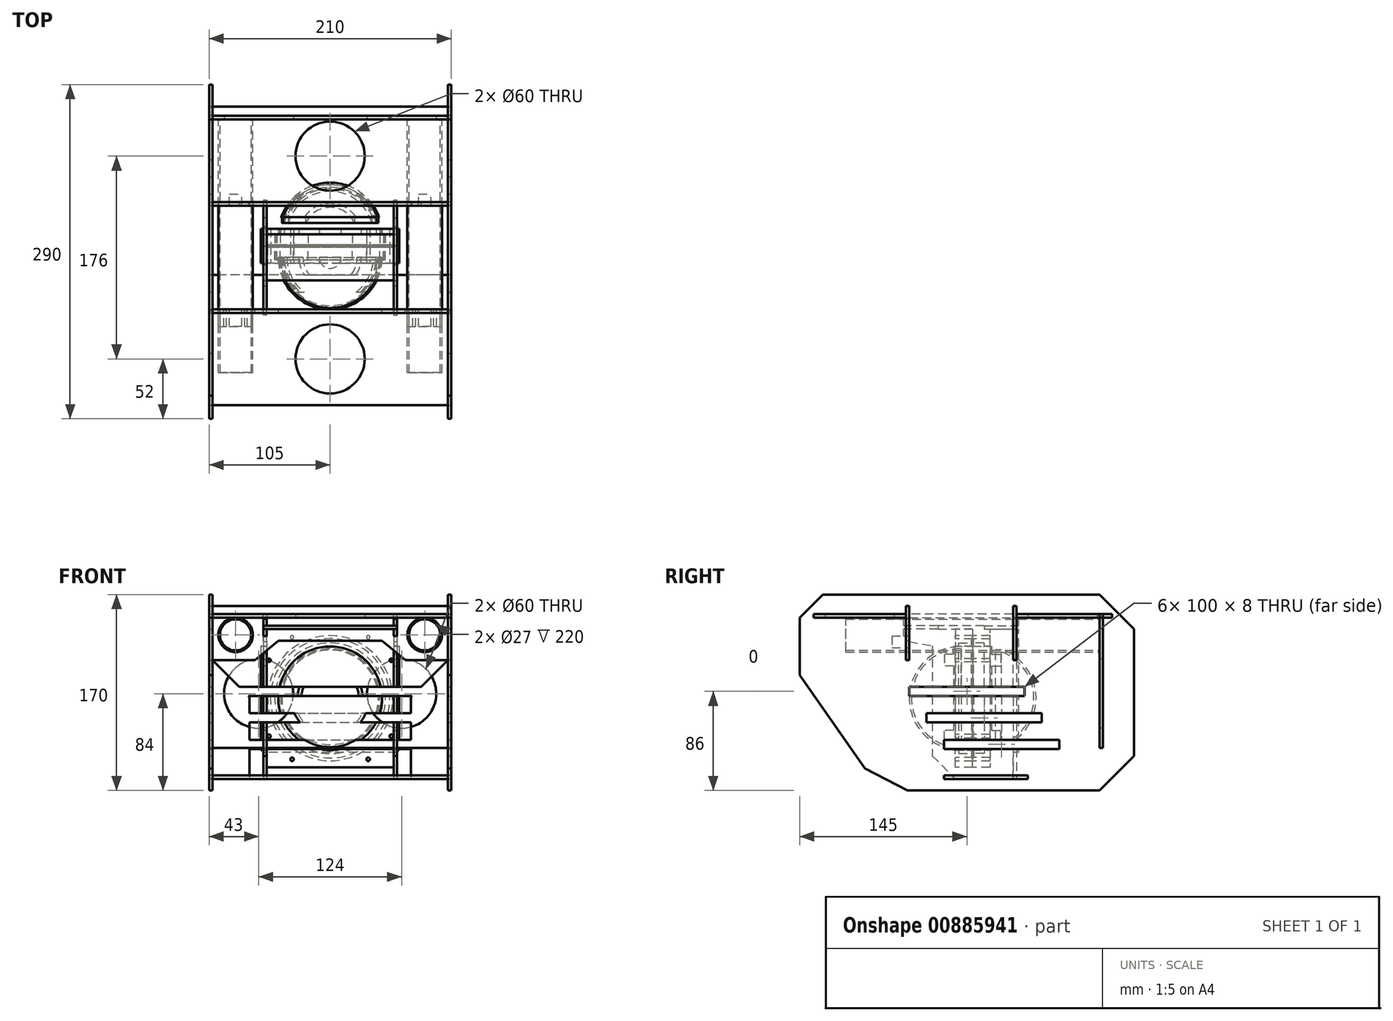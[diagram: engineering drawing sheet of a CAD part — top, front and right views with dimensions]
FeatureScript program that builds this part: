
annotation { "Feature Type Name" : "Feature", "Feature Type Description" : "" }
export const myFeature = defineFeature(function(context is Context, id is Id, definition is map)
    precondition{}
    {
        {
            var Q0;
            Q0=qCreatedBy(makeId("Front.planeOp"),FACE);
            var sketch = newSketch(context, id + "F0", { "sketchPlane" : qUnion([Q0])});
            skArc(sketch, "E0", {"start": v(0, 45) * mm, "mid": v(-45, 0) * mm, "end": v(0, -45) * mm});
            skLineSegment(sketch, "E1", {"start": v(0, 45) * mm, "end": v(0, -45) * mm});
            skSolve(sketch);
        }
        {
            var Q0;
            Q0=makeQuery(id+"F0.imprint","IMPRINT",FACE,{"disambiguationData":[TD([[makeQuery(id+"F0.imprint","IMPRINT",EDGE,{"derivedFrom":sQuery(id+"F0.wireOp",EDGE,"E0")}),1.0]])]});
            var Q1;
            Q1=sQuery(id+"F0.wireOp",EDGE,"E1");
            revolve(context, id + "F1", {"surfaceOperationType" : NewSurfaceOperationType.NEW, "entities" : qUnion([Q0]), "axis" : qUnion([Q1]), "revolveType" : RevolveType.ONE_DIRECTION, "oppositeDirection" : true, "angle" : 180 * degree});
        }
        {
            var Q0;
            Q0=qCreatedBy(makeId("Front.planeOp"),FACE);
            var sketch = newSketch(context, id + "F2", { "sketchPlane" : qUnion([Q0])});
            skArc(sketch, "E2", {"start": v(0, 43) * mm, "mid": v(-43, 0) * mm, "end": v(0, -43) * mm});
            skLineSegment(sketch, "E3", {"start": v(0, 43) * mm, "end": v(0, -43) * mm});
            skSolve(sketch);
        }
        {
            var Q0;
            Q0=makeQuery(id+"F2.imprint","IMPRINT",FACE,{"disambiguationData":[TD([[makeQuery(id+"F2.imprint","IMPRINT",EDGE,{"derivedFrom":sQuery(id+"F2.wireOp",EDGE,"E2")}),1.0]])]});
            var Q1;
            Q1=sQuery(id+"F2.wireOp",EDGE,"E3");
            revolve(context, id + "F3", {"operationType" : NewBodyOperationType.REMOVE, "surfaceOperationType" : NewSurfaceOperationType.NEW, "entities" : qUnion([Q0]), "axis" : qUnion([Q1]), "revolveType" : RevolveType.FULL, "oppositeDirection" : true});
        }
        {
            var Q0;
            Q0=qCreatedBy(makeId("Front.planeOp"),FACE);
            var sketch = newSketch(context, id + "F4", { "sketchPlane" : qUnion([Q0])});
            skCircle(sketch, "E4", {"center": v(0, 0) * mm, "radius": 43 * mm});
            skCircle(sketch, "E5", {"center": v(0, 0) * mm, "radius": 48 * mm});
            skSolve(sketch);
        }
        {
            var Q0;
            Q0 = qSketchRegion(id + "F4", true);
            extrude(context, id + "F5", {"entities" : qUnion([Q0]), "operationType" : NewBodyOperationType.ADD, "depth" : 2 * mm, "offsetDistance" : 25 * mm});
        }
        {
            var Q0;
            Q0=qCreatedBy(makeId("Front.planeOp"),FACE);
            var sketch = newSketch(context, id + "F6", { "sketchPlane" : qUnion([Q0])});
            skCircle(sketch, "E6", {"center": v(0, 0) * mm, "radius": 45 * mm});
            skLineSegment(sketch, "E7.bottom", {"start": v(60, 60) * mm, "end": v(-60, 60) * mm});
            skLineSegment(sketch, "E7.top", {"start": v(60, -60) * mm, "end": v(-60, -60) * mm});
            skLineSegment(sketch, "E7.left", {"start": v(60, 60) * mm, "end": v(60, -60) * mm});
            skLineSegment(sketch, "E7.right", {"start": v(-60, 60) * mm, "end": v(-60, -60) * mm});
            skSolve(sketch);
        }
        {
            var Q0;
            Q0 = qSketchRegion(id + "F6", true);
            extrude(context, id + "F7", {"entities" : qUnion([Q0]), "depth" : 5 * mm, "offsetDistance" : 25 * mm, "hasSecondDirection" : true, "secondDirectionOppositeDirection" : true, "secondDirectionDepth" : 10 * mm});
        }
        {
            var Q0;
            Q0=makeQuery(id+"F7.opExtrude","CAP_FACE",FACE,{"disambiguationData":[OSD([sQuery(id+"F6.wireOp",EDGE,"E6"),sQuery(id+"F6.wireOp",EDGE,"E7.bottom"),sQuery(id+"F6.wireOp",EDGE,"E7.top"),sQuery(id+"F6.wireOp",EDGE,"E7.left"),sQuery(id+"F6.wireOp",EDGE,"E7.right")])],"isStart":true});
            var sketch = newSketch(context, id + "F8", { "sketchPlane" : qUnion([Q0])});
            skCircle(sketch, "E8", {"center": v(0, 0) * mm, "radius": 45 * mm});
            skCircle(sketch, "E9", {"center": v(0, 0) * mm, "radius": 48 * mm});
            skSolve(sketch);
        }
        {
            var Q0;
            Q0 = qSketchRegion(id + "F8", true);
            extrude(context, id + "F9", {"entities" : qUnion([Q0]), "operationType" : NewBodyOperationType.REMOVE, "oppositeDirection" : true, "depth" : 12 * mm, "offsetDistance" : 25 * mm});
        }
        {
            var Q0;
            Q0=qCreatedBy(makeId("Front.planeOp"),FACE);
            var sketch = newSketch(context, id + "F10", { "sketchPlane" : qUnion([Q0])});
            skCircle(sketch, "E10", {"center": v(53, -33) * mm, "radius": 1.5 * mm});
            skCircle(sketch, "E11", {"center": v(33, -53) * mm, "radius": 1.5 * mm});
            skCircle(sketch, "E12.MirrorC", {"center": v(53, 33) * mm, "radius": 1.5 * mm});
            skCircle(sketch, "E13.MirrorC", {"center": v(33, 53) * mm, "radius": 1.5 * mm});
            skCircle(sketch, "E14.MirrorC", {"center": v(-33, -53) * mm, "radius": 1.5 * mm});
            skCircle(sketch, "E15.MirrorC", {"center": v(-53, -33) * mm, "radius": 1.5 * mm});
            skCircle(sketch, "E16.MirrorC", {"center": v(-53, 33) * mm, "radius": 1.5 * mm});
            skCircle(sketch, "E17.MirrorC", {"center": v(-33, 53) * mm, "radius": 1.5 * mm});
            skSolve(sketch);
        }
        {
            var Q0;
            Q0 = qSketchRegion(id + "F10", true);
            extrude(context, id + "F11", {"entities" : qUnion([Q0]), "operationType" : NewBodyOperationType.REMOVE, "endBound" : BoundingType.SYMMETRIC, "oppositeDirection" : true, "depth" : 50 * mm, "offsetDistance" : 25 * mm});
        }
        {
            var Q0;
            Q0=makeQuery(id+"F7.opExtrude","CAP_FACE",FACE,{"disambiguationData":[OSD([sQuery(id+"F6.wireOp",EDGE,"E6"),sQuery(id+"F6.wireOp",EDGE,"E7.bottom"),sQuery(id+"F6.wireOp",EDGE,"E7.top"),sQuery(id+"F6.wireOp",EDGE,"E7.left"),sQuery(id+"F6.wireOp",EDGE,"E7.right")])],"isStart":true});
            var sketch = newSketch(context, id + "F12", { "sketchPlane" : qUnion([Q0])});
            skCircle(sketch, "E18", {"center": v(0, 0) * mm, "radius": 69 * mm});
            skSolve(sketch);
        }
        {
            var Q0;
            Q0=qCreatedBy(makeId("Top.planeOp"),FACE);
            var sketch = newSketch(context, id + "F13", { "sketchPlane" : qUnion([Q0])});
            skCircle(sketch, "E19", {"center": v(53, 10) * mm, "radius": 1.25 * mm, "construction": true});
            skLineSegment(sketch, "E20.bottom", {"start": v(54.25, 9) * mm, "end": v(51.75, 9) * mm});
            skLineSegment(sketch, "E20.top", {"start": v(54.25, 11) * mm, "end": v(51.75, 11) * mm});
            skLineSegment(sketch, "E20.left", {"start": v(54.25, 9) * mm, "end": v(54.25, 11) * mm});
            skLineSegment(sketch, "E20.right", {"start": v(51.75, 9) * mm, "end": v(51.75, 11) * mm});
            skSolve(sketch);
        }
        {
            var Q0;
            Q0 = qSketchRegion(id + "F13", true);
            var Q1;
            Q1=sQuery(id+"F12.wireOp",EDGE,"E18");
            sweep(context, id + "F14", {"operationType" : NewBodyOperationType.REMOVE, "profiles" : qUnion([Q0]), "path" : qUnion([Q1])});
        }
        {
            var Q0;
            {var subQ0=sQuery(id+"F6.wireOp",EDGE,"E7.right");var subQ1=sQuery(id+"F6.wireOp",EDGE,"E7.left");var subQ2=sQuery(id+"F6.wireOp",EDGE,"E7.top");var subQ3=sQuery(id+"F6.wireOp",EDGE,"E7.bottom");Q0=makeQuery(id+"F14.boolean.opBoolean","SPLIT",FACE,{"disambiguationData":[TD([makeQuery(id+"F7.opExtrude","SWEPT_FACE",FACE,{"disambiguationData":[OSD([subQ3])]})])],"derivedFrom":makeQuery(id+"F7.opExtrude","CAP_FACE",FACE,{"disambiguationData":[OSD([sQuery(id+"F6.wireOp",EDGE,"E6"),subQ3,subQ2,subQ1,subQ0])],"isStart":true})});}
            var sketch = newSketch(context, id + "F15", { "sketchPlane" : qUnion([Q0])});
            skLineSegment(sketch, "E21.bottom", {"start": v(-60, -60) * mm, "end": v(60, -60) * mm});
            skLineSegment(sketch, "E21.top", {"start": v(-60, 60) * mm, "end": v(60, 60) * mm});
            skLineSegment(sketch, "E21.left", {"start": v(-60, -60) * mm, "end": v(-60, 60) * mm});
            skLineSegment(sketch, "E21.right", {"start": v(60, -60) * mm, "end": v(60, 60) * mm});
            skCircle(sketch, "E22", {"center": v(0, 0) * mm, "radius": 60 * mm});
            skSolve(sketch);
        }
        {
            var Q0;
            Q0 = qSketchRegion(id + "F15", true);
            extrude(context, id + "F16", {"entities" : qUnion([Q0]), "depth" : 15 * mm, "offsetDistance" : 25 * mm});
        }
        {
            var Q0;
            Q0=qCreatedBy(makeId("Front.planeOp"),FACE);
            cPlane(context, id + "F17", {"entities" : qUnion([Q0]), "cplaneType" : CPlaneType.OFFSET, "offset" : 20 * mm, "oppositeDirection" : true, "width" : 150 * mm, "height" : 150 * mm});
        }
        {
            var Q0;
            Q0 = qSketchRegion(id + "F8", true);
            extrude(context, id + "F18", {"entities" : qUnion([Q0]), "operationType" : NewBodyOperationType.REMOVE, "depth" : 12 * mm, "offsetDistance" : 25 * mm});
        }
        {
            var Q0;
            Q0=qCreatedBy(id+"F17.planeOp",FACE);
            var sketch = newSketch(context, id + "F19", { "sketchPlane" : qUnion([Q0])});
            skArc(sketch, "E23", {"start": v(-45, 0) * mm, "mid": v(0, -45) * mm, "end": v(45, 0) * mm});
            skLineSegment(sketch, "E24", {"start": v(-45, 0) * mm, "end": v(45, 0) * mm});
            skSolve(sketch);
        }
        {
            var Q0;
            Q0 = qSketchRegion(id + "F19", true);
            var Q1;
            Q1=sQuery(id+"F19.wireOp",EDGE,"E24");
            revolve(context, id + "F20", {"surfaceOperationType" : NewSurfaceOperationType.NEW, "entities" : qUnion([Q0]), "axis" : qUnion([Q1]), "revolveType" : RevolveType.ONE_DIRECTION, "angle" : 180 * degree});
        }
        {
            var Q0;
            Q0=makeQuery(id+"F20.opRevolve","CAP_FACE",FACE,{"disambiguationData":[OSD([sQuery(id+"F19.wireOp",EDGE,"E23"),sQuery(id+"F19.wireOp",EDGE,"E24")])],"isStart":true});
            var sketch = newSketch(context, id + "F21", { "sketchPlane" : qUnion([Q0])});
            skArc(sketch, "E25", {"start": v(-43, 0) * mm, "mid": v(0, -43) * mm, "end": v(43, 0) * mm});
            skLineSegment(sketch, "E26", {"start": v(-43, 0) * mm, "end": v(43, 0) * mm});
            skSolve(sketch);
        }
        {
            var Q0;
            Q0 = qSketchRegion(id + "F21", true);
            var Q1;
            Q1=sQuery(id+"F21.wireOp",EDGE,"E26");
            revolve(context, id + "F22", {"operationType" : NewBodyOperationType.REMOVE, "surfaceOperationType" : NewSurfaceOperationType.NEW, "entities" : qUnion([Q0]), "axis" : qUnion([Q1]), "revolveType" : RevolveType.FULL, "oppositeDirection" : true});
        }
        {
            var Q0;
            Q0=makeQuery(id+"F20.opRevolve","CAP_FACE",FACE,{"disambiguationData":[OSD([sQuery(id+"F19.wireOp",EDGE,"E23"),sQuery(id+"F19.wireOp",EDGE,"E24")])],"isStart":true});
            var sketch = newSketch(context, id + "F23", { "sketchPlane" : qUnion([Q0])});
            skCircle(sketch, "E27", {"center": v(0, 0) * mm, "radius": 43 * mm});
            skCircle(sketch, "E28", {"center": v(0, 0) * mm, "radius": 48 * mm});
            skSolve(sketch);
        }
        {
            var Q0;
            Q0 = qSketchRegion(id + "F23", true);
            extrude(context, id + "F24", {"entities" : qUnion([Q0]), "operationType" : NewBodyOperationType.ADD, "oppositeDirection" : true, "depth" : 2 * mm, "offsetDistance" : 25 * mm});
        }
        {
            var Q0;
            Q0 = qSketchRegion(id + "F13", true);
            var Q1;
            Q1 = qConstructionFilter(qBodyType(qCreatedBy(id + "F12" ,EDGE), BodyType.WIRE), ConstructionObject.NO);
            sweep(context, id + "F25", {"operationType" : NewBodyOperationType.REMOVE, "profiles" : qUnion([Q0]), "path" : qUnion([Q1])});
        }
        {
            var Q0;
            Q0 = qSketchRegion(id + "F10", true);
            extrude(context, id + "F26", {"entities" : qUnion([Q0]), "operationType" : NewBodyOperationType.REMOVE, "oppositeDirection" : true, "depth" : 25 * mm, "offsetDistance" : 25 * mm});
        }
        {
            var Q0;
            Q0=qCreatedBy(makeId("Front.planeOp"),FACE);
            var sketch = newSketch(context, id + "F27", { "sketchPlane" : qUnion([Q0])});
            skLineSegment(sketch, "E29.bottom", {"start": v(85, 60) * mm, "end": v(55, 60) * mm});
            skLineSegment(sketch, "E29.top", {"start": v(85, 45) * mm, "end": v(55, 45) * mm});
            skLineSegment(sketch, "E29.left", {"start": v(85, 60) * mm, "end": v(85, 45) * mm});
            skLineSegment(sketch, "E29.right", {"start": v(55, 60) * mm, "end": v(55, 45) * mm});
            skLineSegment(sketch, "E30.MirrorCS", {"start": v(-85, 60) * mm, "end": v(-85, 45) * mm});
            skLineSegment(sketch, "E31.MirrorCS", {"start": v(-55, 60) * mm, "end": v(-55, 45) * mm});
            skLineSegment(sketch, "E32.MirrorCS", {"start": v(-85, 60) * mm, "end": v(-55, 60) * mm});
            skLineSegment(sketch, "E33.MirrorCS", {"start": v(-85, 45) * mm, "end": v(-55, 45) * mm});
            skLineSegment(sketch, "E34.MirrorCS", {"start": v(-55, -60) * mm, "end": v(-55, -45) * mm});
            skLineSegment(sketch, "E35.MirrorCS", {"start": v(85, -45) * mm, "end": v(55, -45) * mm});
            skLineSegment(sketch, "E36.MirrorCS", {"start": v(-85, -45) * mm, "end": v(-55, -45) * mm});
            skLineSegment(sketch, "E37.MirrorCS", {"start": v(85, -60) * mm, "end": v(85, -45) * mm});
            skLineSegment(sketch, "E38.MirrorCS", {"start": v(85, -60) * mm, "end": v(55, -60) * mm});
            skLineSegment(sketch, "E39.MirrorCS", {"start": v(-85, -60) * mm, "end": v(-55, -60) * mm});
            skLineSegment(sketch, "E40.MirrorCS", {"start": v(-85, -60) * mm, "end": v(-85, -45) * mm});
            skLineSegment(sketch, "E41.MirrorCS", {"start": v(55, -60) * mm, "end": v(55, -45) * mm});
            skSolve(sketch);
        }
        {
            var Q0;
            Q0 = qSketchRegion(id + "F27", true);
            extrude(context, id + "F28", {"entities" : qUnion([Q0]), "operationType" : NewBodyOperationType.REMOVE, "endBound" : BoundingType.SYMMETRIC, "oppositeDirection" : true, "depth" : 500 * mm, "offsetDistance" : 25 * mm});
        }
        {
            var Q0;
            Q0=qCreatedBy(makeId("Right.planeOp"),FACE);
            cPlane(context, id + "F29", {"entities" : qUnion([Q0]), "cplaneType" : CPlaneType.OFFSET, "offset" : 56.5 * mm, "width" : 150 * mm, "height" : 150 * mm});
        }
        {
            var Q0;
            Q0=qCreatedBy(id+"F29.planeOp",FACE);
            var sketch = newSketch(context, id + "F30", { "sketchPlane" : qUnion([Q0])});
            skLineSegment(sketch, "E42.bottom", {"start": v(-6.5, 45) * mm, "end": v(26.5, 45) * mm});
            skLineSegment(sketch, "E42.top", {"start": v(-6.5, -45) * mm, "end": v(26.5, -45) * mm});
            skLineSegment(sketch, "E42.left", {"start": v(-6.5, 45) * mm, "end": v(-6.5, -45) * mm});
            skLineSegment(sketch, "E42.right", {"start": v(26.5, 45) * mm, "end": v(26.5, -45) * mm});
            skLineSegment(sketch, "E43", {"start": v(-50, 73) * mm, "end": v(-50, 50) * mm});
            skLineSegment(sketch, "E44", {"start": v(-5, -70) * mm, "end": v(50, -70) * mm});
            skLineSegment(sketch, "E45", {"start": v(50, -70) * mm, "end": v(50, 73) * mm});
            skLineSegment(sketch, "E46", {"start": v(50, 73) * mm, "end": v(-50, 73) * mm});
            skLineSegment(sketch, "E47", {"start": v(-50, 50) * mm, "end": v(-25, 45.6) * mm});
            skLineSegment(sketch, "E48", {"start": v(-25, 45.6) * mm, "end": v(-25, -50) * mm});
            skLineSegment(sketch, "E49", {"start": v(-25, -50) * mm, "end": v(-5, -70) * mm});
            skSolve(sketch);
        }
        {
            var Q0;
            Q0 = qSketchRegion(id + "F30", true);
            extrude(context, id + "F31", {"entities" : qUnion([Q0]), "endBound" : BoundingType.SYMMETRIC, "depth" : 3 * mm, "offsetDistance" : 25 * mm});
        }
        {
            var Q0;
            Q0=qCreatedBy(id+"F29.planeOp",FACE);
            var sketch = newSketch(context, id + "F32", { "sketchPlane" : qUnion([Q0])});
            skLineSegment(sketch, "E50.bottom", {"start": v(26.5, 38) * mm, "end": v(34.5, 38) * mm});
            skLineSegment(sketch, "E50.top", {"start": v(26.5, 28) * mm, "end": v(34.5, 28) * mm});
            skLineSegment(sketch, "E50.left", {"start": v(26.5, 38) * mm, "end": v(26.5, 28) * mm});
            skLineSegment(sketch, "E50.right", {"start": v(34.5, 38) * mm, "end": v(34.5, 28) * mm});
            skLineSegment(sketch, "E51.MirrorCS", {"start": v(34.5, -38) * mm, "end": v(34.5, -28) * mm});
            skLineSegment(sketch, "E52.MirrorCS", {"start": v(26.5, -28) * mm, "end": v(34.5, -28) * mm});
            skLineSegment(sketch, "E53.MirrorCS", {"start": v(26.5, -38) * mm, "end": v(34.5, -38) * mm});
            skLineSegment(sketch, "E54.MirrorCS", {"start": v(26.5, -38) * mm, "end": v(26.5, -28) * mm});
            skLineSegment(sketch, "E55.MirrorCS", {"start": v(-6.5, 28) * mm, "end": v(-14.5, 28) * mm});
            skLineSegment(sketch, "E56.MirrorCS", {"start": v(-6.5, -38) * mm, "end": v(-14.5, -38) * mm});
            skLineSegment(sketch, "E57.MirrorCS", {"start": v(-6.5, -28) * mm, "end": v(-14.5, -28) * mm});
            skLineSegment(sketch, "E58.MirrorCS", {"start": v(-6.5, 38) * mm, "end": v(-14.5, 38) * mm});
            skLineSegment(sketch, "E59.MirrorCS", {"start": v(-14.5, 38) * mm, "end": v(-14.5, 28) * mm});
            skLineSegment(sketch, "E60.MirrorCS", {"start": v(-6.5, 38) * mm, "end": v(-6.5, 28) * mm});
            skLineSegment(sketch, "E61.MirrorCS", {"start": v(-6.5, -38) * mm, "end": v(-6.5, -28) * mm});
            skLineSegment(sketch, "E62.MirrorCS", {"start": v(-14.5, -38) * mm, "end": v(-14.5, -28) * mm});
            skSolve(sketch);
        }
        {
            var Q0;
            Q0 = qSketchRegion(id + "F32", true);
            extrude(context, id + "F33", {"entities" : qUnion([Q0]), "operationType" : NewBodyOperationType.REMOVE, "endBound" : BoundingType.SYMMETRIC, "oppositeDirection" : true, "depth" : 25 * mm, "offsetDistance" : 25 * mm});
        }
        {
            var Q0;
            Q0=makeQuery(id+"F31.opExtrude","SWEPT_BODY",BODY,{"disambiguationData":[OSD([sQuery(id+"F30.wireOp",EDGE,"E42.bottom"),sQuery(id+"F30.wireOp",EDGE,"E42.top"),sQuery(id+"F30.wireOp",EDGE,"E42.left"),sQuery(id+"F30.wireOp",EDGE,"E42.right"),sQuery(id+"F30.wireOp",EDGE,"E43"),sQuery(id+"F30.wireOp",EDGE,"E44"),sQuery(id+"F30.wireOp",EDGE,"E45"),sQuery(id+"F30.wireOp",EDGE,"E46"),sQuery(id+"F30.wireOp",EDGE,"E47"),sQuery(id+"F30.wireOp",EDGE,"E48"),sQuery(id+"F30.wireOp",EDGE,"E49")])]});
            var Q1;
            Q1=qCreatedBy(makeId("Right.planeOp"),FACE);
            mirror(context, id + "F34", {"entities" : qUnion([Q0]), "mirrorPlane" : qUnion([Q1])});
        }
        {
            var Q0;
            Q0=qCreatedBy(makeId("Top.planeOp"),FACE);
            cPlane(context, id + "F35", {"entities" : qUnion([Q0]), "cplaneType" : CPlaneType.OFFSET, "offset" : 60 * mm, "width" : 150 * mm, "height" : 150 * mm});
        }
        {
            var Q0;
            Q0=qCreatedBy(id+"F35.planeOp",FACE);
            var sketch = newSketch(context, id + "F36", { "sketchPlane" : qUnion([Q0])});
            skLineSegment(sketch, "E63.bottom", {"start": v(55, -50) * mm, "end": v(-55, -50) * mm});
            skLineSegment(sketch, "E63.top", {"start": v(55, 50) * mm, "end": v(-55, 50) * mm});
            skLineSegment(sketch, "E63.left", {"start": v(55, -50) * mm, "end": v(55, 50) * mm});
            skLineSegment(sketch, "E63.right", {"start": v(-55, -50) * mm, "end": v(-55, 50) * mm});
            skSolve(sketch);
        }
        {
            var Q0;
            Q0 = qSketchRegion(id + "F36", true);
            extrude(context, id + "F37", {"entities" : qUnion([Q0]), "depth" : 3 * mm, "offsetDistance" : 25 * mm});
        }
        {
            var Q0;
            Q0=qCreatedBy(id+"F35.planeOp",FACE);
            var sketch = newSketch(context, id + "F38", { "sketchPlane" : qUnion([Q0])});
            skLineSegment(sketch, "E64.bottom", {"start": v(55, -50) * mm, "end": v(58, -50) * mm});
            skLineSegment(sketch, "E64.top", {"start": v(55, -20) * mm, "end": v(58, -20) * mm});
            skLineSegment(sketch, "E64.left", {"start": v(55, -50) * mm, "end": v(55, -20) * mm});
            skLineSegment(sketch, "E64.right", {"start": v(58, -50) * mm, "end": v(58, -20) * mm});
            skLineSegment(sketch, "E65.bottom", {"start": v(55, 20) * mm, "end": v(58, 20) * mm});
            skLineSegment(sketch, "E65.top", {"start": v(55, 50) * mm, "end": v(58, 50) * mm});
            skLineSegment(sketch, "E65.left", {"start": v(55, 20) * mm, "end": v(55, 50) * mm});
            skLineSegment(sketch, "E65.right", {"start": v(58, 20) * mm, "end": v(58, 50) * mm});
            skLineSegment(sketch, "E66.MirrorCS", {"start": v(-55, -20) * mm, "end": v(-58, -20) * mm});
            skLineSegment(sketch, "E67.MirrorCS", {"start": v(-55, 50) * mm, "end": v(-58, 50) * mm});
            skLineSegment(sketch, "E68.MirrorCS", {"start": v(-55, -50) * mm, "end": v(-58, -50) * mm});
            skLineSegment(sketch, "E69.MirrorCS", {"start": v(-55, 20) * mm, "end": v(-58, 20) * mm});
            skLineSegment(sketch, "E70.MirrorCS", {"start": v(-55, 20) * mm, "end": v(-55, 50) * mm});
            skLineSegment(sketch, "E71.MirrorCS", {"start": v(-55, -50) * mm, "end": v(-55, -20) * mm});
            skLineSegment(sketch, "E72.MirrorCS", {"start": v(-58, -50) * mm, "end": v(-58, -20) * mm});
            skLineSegment(sketch, "E73.MirrorCS", {"start": v(-58, 20) * mm, "end": v(-58, 50) * mm});
            skSolve(sketch);
        }
        {
            var Q0;
            Q0 = qSketchRegion(id + "F38", true);
            extrude(context, id + "F39", {"entities" : qUnion([Q0]), "operationType" : NewBodyOperationType.ADD, "depth" : 3 * mm, "offsetDistance" : 25 * mm});
        }
        {
            var Q0;
            Q0=qCreatedBy(makeId("Right.planeOp"),FACE);
            var sketch = newSketch(context, id + "F40", { "sketchPlane" : qUnion([Q0])});
            skLineSegment(sketch, "E74.bottom", {"start": v(-20, 63) * mm, "end": v(-60, 63) * mm});
            skLineSegment(sketch, "E74.top", {"start": v(-20, 60) * mm, "end": v(-60, 60) * mm});
            skLineSegment(sketch, "E74.left", {"start": v(-20, 63) * mm, "end": v(-20, 60) * mm});
            skLineSegment(sketch, "E74.right", {"start": v(-60, 63) * mm, "end": v(-60, 60) * mm});
            skLineSegment(sketch, "E75.bottom", {"start": v(20, 63) * mm, "end": v(60, 63) * mm});
            skLineSegment(sketch, "E75.top", {"start": v(20, 60) * mm, "end": v(60, 60) * mm});
            skLineSegment(sketch, "E75.left", {"start": v(20, 63) * mm, "end": v(20, 60) * mm});
            skLineSegment(sketch, "E75.right", {"start": v(60, 63) * mm, "end": v(60, 60) * mm});
            skSolve(sketch);
        }
        {
            var Q0;
            Q0 = qSketchRegion(id + "F40", true);
            extrude(context, id + "F41", {"entities" : qUnion([Q0]), "operationType" : NewBodyOperationType.REMOVE, "endBound" : BoundingType.SYMMETRIC, "oppositeDirection" : true, "depth" : 300 * mm, "offsetDistance" : 25 * mm});
        }
        {
            var Q0;
            Q0=qCreatedBy(makeId("Front.planeOp"),FACE);
            var sketch = newSketch(context, id + "F42", { "sketchPlane" : qUnion([Q0])});
            skCircle(sketch, "E76", {"center": v(82, 55) * mm, "radius": 15 * mm});
            skCircle(sketch, "E77", {"center": v(82, 55) * mm, "radius": 13.5 * mm});
            skCircle(sketch, "E78.MirrorC", {"center": v(-82, 55) * mm, "radius": 15 * mm});
            skCircle(sketch, "E79.MirrorC", {"center": v(-82, 55) * mm, "radius": 13.5 * mm});
            skSolve(sketch);
        }
        {
            var Q0;
            Q0 = qSketchRegion(id + "F42", true);
            extrude(context, id + "F43", {"entities" : qUnion([Q0]), "depth" : 100 * mm, "offsetDistance" : 25 * mm, "hasSecondDirection" : true, "secondDirectionOppositeDirection" : true, "secondDirectionDepth" : 120 * mm});
        }
        {
            var Q0;
            Q0=qCreatedBy(makeId("Right.planeOp"),FACE);
            cPlane(context, id + "F44", {"entities" : qUnion([Q0]), "cplaneType" : CPlaneType.OFFSET, "offset" : 120 * mm, "width" : 150 * mm, "height" : 150 * mm});
        }
        {
            var Q0;
            Q0=makeQuery(id+"F18.boolean.opBoolean","SPLIT",FACE,{"disambiguationData":[TD([makeQuery(id+"F18.opExtrude","SWEPT_FACE",FACE,{"disambiguationData":[OSD([sQuery(id+"F8.wireOp",EDGE,"E8")])]})])],"derivedFrom":makeQuery(id+"F16.opExtrude","CAP_FACE",FACE,{"disambiguationData":[OSD([sQuery(id+"F15.wireOp",EDGE,"E21.bottom"),sQuery(id+"F15.wireOp",EDGE,"E21.top"),sQuery(id+"F15.wireOp",EDGE,"E21.left"),sQuery(id+"F15.wireOp",EDGE,"E21.right")])],"isStart":true})});
            extrude(context, id + "F45", {"entities" : qUnion([Q0]), "operationType" : NewBodyOperationType.REMOVE, "oppositeDirection" : true, "depth" : 25 * mm, "offsetDistance" : 25 * mm});
        }
        {
            var Q0;
            Q0=qCreatedBy(makeId("Front.planeOp"),FACE);
            cPlane(context, id + "F46", {"entities" : qUnion([Q0]), "cplaneType" : CPlaneType.OFFSET, "offset" : 45 * mm, "width" : 150 * mm, "height" : 150 * mm});
        }
        {
            var Q0;
            Q0=qCreatedBy(makeId("Right.planeOp"),FACE);
            var sketch = newSketch(context, id + "F47", { "sketchPlane" : qUnion([Q0])});
            skLineSegment(sketch, "E80.bottom", {"start": v(-60, 69) * mm, "end": v(-45, 69) * mm});
            skLineSegment(sketch, "E80.top", {"start": v(-60, 79) * mm, "end": v(-45, 79) * mm});
            skLineSegment(sketch, "E80.left", {"start": v(-60, 79) * mm, "end": v(-60, 69) * mm});
            skLineSegment(sketch, "E80.right", {"start": v(-45, 79) * mm, "end": v(-45, 69) * mm});
            skLineSegment(sketch, "E81.bottom", {"start": v(-45, 54) * mm, "end": v(-60, 54) * mm});
            skLineSegment(sketch, "E81.top", {"start": v(-45, 44) * mm, "end": v(-60, 44) * mm});
            skLineSegment(sketch, "E81.left", {"start": v(-45, 54) * mm, "end": v(-45, 44) * mm});
            skLineSegment(sketch, "E81.right", {"start": v(-60, 54) * mm, "end": v(-60, 44) * mm});
            skLineSegment(sketch, "E82.bottom", {"start": v(45, 79) * mm, "end": v(55, 79) * mm});
            skLineSegment(sketch, "E82.top", {"start": v(45, 69) * mm, "end": v(55, 69) * mm});
            skLineSegment(sketch, "E82.left", {"start": v(45, 69) * mm, "end": v(45, 79) * mm});
            skLineSegment(sketch, "E82.right", {"start": v(55, 69) * mm, "end": v(55, 79) * mm});
            skLineSegment(sketch, "E83.bottom", {"start": v(45, -47) * mm, "end": v(55, -47) * mm});
            skLineSegment(sketch, "E83.top", {"start": v(45, -82) * mm, "end": v(55, -82) * mm});
            skLineSegment(sketch, "E83.left", {"start": v(45, -47) * mm, "end": v(45, -82) * mm});
            skLineSegment(sketch, "E83.right", {"start": v(55, -47) * mm, "end": v(55, -82) * mm});
            skSolve(sketch);
        }
        {
            var Q0;
            Q0 = qSketchRegion(id + "F47", true);
            extrude(context, id + "F48", {"entities" : qUnion([Q0]), "operationType" : NewBodyOperationType.REMOVE, "endBound" : BoundingType.SYMMETRIC, "oppositeDirection" : true, "depth" : 200 * mm, "offsetDistance" : 25 * mm});
        }
        {
            var Q0;
            Q0=qCreatedBy(id+"F46.planeOp",FACE);
            var sketch = newSketch(context, id + "F49", { "sketchPlane" : qUnion([Q0])});
            skLineSegment(sketch, "E84", {"start": v(0, 80) * mm, "end": v(-105, 80) * mm});
            skLineSegment(sketch, "E85", {"start": v(-105, 80) * mm, "end": v(-105, 33) * mm});
            skLineSegment(sketch, "E86", {"start": v(-105, 33) * mm, "end": v(-65.26, 33) * mm});
            skLineSegment(sketch, "E87", {"start": v(-65.26, 33) * mm, "end": v(-45, 50) * mm});
            skLineSegment(sketch, "E88", {"start": v(-45, 50) * mm, "end": v(0, 50) * mm});
            skCircle(sketch, "E89", {"center": v(-82, 55) * mm, "radius": 15 * mm});
            skCircle(sketch, "E90.MirrorC", {"center": v(82, 55) * mm, "radius": 15 * mm});
            skLineSegment(sketch, "E91.MirrorCS", {"start": v(45, 50) * mm, "end": v(0, 50) * mm});
            skLineSegment(sketch, "E92.MirrorCS", {"start": v(0, 80) * mm, "end": v(105, 80) * mm});
            skLineSegment(sketch, "E93.MirrorCS", {"start": v(105, 33) * mm, "end": v(65.26, 33) * mm});
            skLineSegment(sketch, "E94.MirrorCS", {"start": v(105, 80) * mm, "end": v(105, 33) * mm});
            skLineSegment(sketch, "E95.MirrorCS", {"start": v(65.26, 33) * mm, "end": v(45, 50) * mm});
            skLineSegment(sketch, "E96", {"start": v(0, 63) * mm, "end": v(-55, 63) * mm});
            skLineSegment(sketch, "E97", {"start": v(-55, 63) * mm, "end": v(-55, 69) * mm});
            skLineSegment(sketch, "E98", {"start": v(-55, 69) * mm, "end": v(-58, 69) * mm});
            skLineSegment(sketch, "E99", {"start": v(-58, 69) * mm, "end": v(-58, 54) * mm});
            skLineSegment(sketch, "E100", {"start": v(-58, 54) * mm, "end": v(-55, 54) * mm});
            skLineSegment(sketch, "E101", {"start": v(-55, 54) * mm, "end": v(-55, 60) * mm});
            skLineSegment(sketch, "E102", {"start": v(-55, 60) * mm, "end": v(0, 60) * mm});
            skLineSegment(sketch, "E103.MirrorCS", {"start": v(58, 69) * mm, "end": v(58, 54) * mm});
            skLineSegment(sketch, "E104.MirrorCS", {"start": v(0, 63) * mm, "end": v(55, 63) * mm});
            skLineSegment(sketch, "E105.MirrorCS", {"start": v(55, 69) * mm, "end": v(58, 69) * mm});
            skLineSegment(sketch, "E106.MirrorCS", {"start": v(55, 63) * mm, "end": v(55, 69) * mm});
            skLineSegment(sketch, "E107.MirrorCS", {"start": v(55, 60) * mm, "end": v(0, 60) * mm});
            skLineSegment(sketch, "E108.MirrorCS", {"start": v(58, 54) * mm, "end": v(55, 54) * mm});
            skLineSegment(sketch, "E109.MirrorCS", {"start": v(55, 54) * mm, "end": v(55, 60) * mm});
            skSolve(sketch);
        }
        {
            var Q0;
            Q0 = qSketchRegion(id + "F49", true);
            extrude(context, id + "F50", {"entities" : qUnion([Q0]), "depth" : 3 * mm, "offsetDistance" : 25 * mm});
        }
        {
            var Q0;
            Q0=qCreatedBy(id+"F46.planeOp",FACE);
            cPlane(context, id + "F51", {"entities" : qUnion([Q0]), "cplaneType" : CPlaneType.OFFSET, "offset" : 90 * mm, "oppositeDirection" : true, "width" : 150 * mm, "height" : 150 * mm});
        }
        {
            var Q0;
            Q0=qCreatedBy(id+"F51.planeOp",FACE);
            var sketch = newSketch(context, id + "F52", { "sketchPlane" : qUnion([Q0])});
            skLineSegment(sketch, "E110.bottom", {"start": v(105, 80) * mm, "end": v(-105, 80) * mm});
            skLineSegment(sketch, "E110.top", {"start": v(70, -70) * mm, "end": v(-70, -70) * mm});
            skLineSegment(sketch, "E110.left", {"start": v(105, 80) * mm, "end": v(105, 33) * mm});
            skLineSegment(sketch, "E110.right", {"start": v(-105, 80) * mm, "end": v(-105, 33) * mm});
            skLineSegment(sketch, "E111", {"start": v(105, 33) * mm, "end": v(70, 33) * mm});
            skLineSegment(sketch, "E112", {"start": v(70, 33) * mm, "end": v(70, -70) * mm});
            skLineSegment(sketch, "E113.MirrorCS", {"start": v(-105, 33) * mm, "end": v(-70, 33) * mm});
            skLineSegment(sketch, "E114.MirrorCS", {"start": v(-70, 33) * mm, "end": v(-70, -70) * mm});
            skCircle(sketch, "E115", {"center": v(-82, 55) * mm, "radius": 15 * mm});
            skCircle(sketch, "E116.MirrorC", {"center": v(82, 55) * mm, "radius": 15 * mm});
            skLineSegment(sketch, "E117", {"start": v(0, 63) * mm, "end": v(55, 63) * mm});
            skLineSegment(sketch, "E118", {"start": v(55, 63) * mm, "end": v(55, 69) * mm});
            skLineSegment(sketch, "E119", {"start": v(55, 69) * mm, "end": v(58, 69) * mm});
            skLineSegment(sketch, "E120", {"start": v(58, 69) * mm, "end": v(58, -47) * mm});
            skLineSegment(sketch, "E121", {"start": v(58, -47) * mm, "end": v(0, -47) * mm});
            skLineSegment(sketch, "E122.MirrorCS", {"start": v(-55, 63) * mm, "end": v(-55, 69) * mm});
            skLineSegment(sketch, "E123.MirrorCS", {"start": v(-55, 69) * mm, "end": v(-58, 69) * mm});
            skLineSegment(sketch, "E124.MirrorCS", {"start": v(-58, 69) * mm, "end": v(-58, -47) * mm});
            skLineSegment(sketch, "E125.MirrorCS", {"start": v(0, 63) * mm, "end": v(-55, 63) * mm});
            skLineSegment(sketch, "E126.MirrorCS", {"start": v(-58, -47) * mm, "end": v(0, -47) * mm});
            skSolve(sketch);
        }
        {
            var Q0;
            Q0 = qSketchRegion(id + "F52", true);
            extrude(context, id + "F53", {"entities" : qUnion([Q0]), "oppositeDirection" : true, "depth" : 3 * mm, "offsetDistance" : 25 * mm});
        }
        {
            var Q0;
            Q0=makeQuery(id+"F50.opExtrude","SWEPT_FACE",FACE,{"disambiguationData":[OSD([sQuery(id+"F49.wireOp",EDGE,"E94.MirrorCS")])]});
            cPlane(context, id + "F54", {"entities" : qUnion([Q0]), "cplaneType" : CPlaneType.OFFSET, "offset" : 0 * mm, "width" : 150 * mm, "height" : 150 * mm});
        }
        {
            var Q0;
            Q0=qCreatedBy(id+"F54.planeOp",FACE);
            var sketch = newSketch(context, id + "F55", { "sketchPlane" : qUnion([Q0])});
            skLineSegment(sketch, "E127.bottom", {"start": v(-140, 90) * mm, "end": v(150, 90) * mm});
            skLineSegment(sketch, "E127.top", {"start": v(-140, -80) * mm, "end": v(150, -80) * mm});
            skLineSegment(sketch, "E127.left", {"start": v(-140, 90) * mm, "end": v(-140, -80) * mm});
            skLineSegment(sketch, "E127.right", {"start": v(150, 90) * mm, "end": v(150, -80) * mm});
            skSolve(sketch);
        }
        {
            var Q0;
            Q0=makeQuery(id+"F55.imprint","IMPRINT",FACE,{"disambiguationData":[TD([[makeQuery(id+"F55.imprint","IMPRINT",EDGE,{"derivedFrom":sQuery(id+"F55.wireOp",EDGE,"E127.bottom")}),-1.0]])]});
            extrude(context, id + "F56", {"entities" : qUnion([Q0]), "oppositeDirection" : true, "depth" : 3 * mm, "offsetDistance" : 25 * mm});
        }
        {
            var Q0;
            Q0=makeQuery(id+"F56.opExtrude","SWEPT_BODY",BODY,{"disambiguationData":[OSD([sQuery(id+"F55.wireOp",EDGE,"E127.bottom"),sQuery(id+"F55.wireOp",EDGE,"E127.top"),sQuery(id+"F55.wireOp",EDGE,"E127.left"),sQuery(id+"F55.wireOp",EDGE,"E127.right")])]});
            var Q1;
            Q1=qCreatedBy(makeId("Right.planeOp"),FACE);
            mirror(context, id + "F57", {"entities" : qUnion([Q0]), "mirrorPlane" : qUnion([Q1])});
        }
        {
            var Q0;
            Q0=makeQuery(id+"F57.opPattern","COPY",EDGE,{"derivedFrom":makeQuery(id+"F56.opExtrude","SWEPT_EDGE",EDGE,{"disambiguationData":[OSD([sQuery(id+"F55.wireOp",EDGE,"E127.bottom"),sQuery(id+"F55.wireOp",EDGE,"E127.left")])]}),"instanceName":"1"});
            var Q1;
            Q1=makeQuery(id+"F56.opExtrude","SWEPT_EDGE",EDGE,{"disambiguationData":[OSD([sQuery(id+"F55.wireOp",EDGE,"E127.bottom"),sQuery(id+"F55.wireOp",EDGE,"E127.left")])]});
            chamfer(context, id + "F58", {"entities" : qUnion([Q0, Q1]), "width" : 20 * mm, "tangentPropagation" : true});
        }
        {
            var Q0;
            Q0=makeQuery(id+"F56.opExtrude","SWEPT_EDGE",EDGE,{"disambiguationData":[OSD([sQuery(id+"F55.wireOp",EDGE,"E127.top"),sQuery(id+"F55.wireOp",EDGE,"E127.left")])]});
            chamfer(context, id + "F59", {"entities" : qUnion([Q0]), "chamferType" : ChamferType.TWO_OFFSETS, "width1" : 100 * mm, "oppositeDirection" : false, "width2" : 70 * mm, "tangentPropagation" : true});
        }
        {
            var Q0;
            Q0=makeQuery(id+"F57.opPattern","COPY",EDGE,{"derivedFrom":makeQuery(id+"F56.opExtrude","SWEPT_EDGE",EDGE,{"disambiguationData":[OSD([sQuery(id+"F55.wireOp",EDGE,"E127.top"),sQuery(id+"F55.wireOp",EDGE,"E127.left")])]}),"instanceName":"1"});
            chamfer(context, id + "F60", {"entities" : qUnion([Q0]), "chamferType" : ChamferType.TWO_OFFSETS, "width1" : 70 * mm, "oppositeDirection" : false, "width2" : 100 * mm, "tangentPropagation" : true});
        }
        {
            var Q0;
            Q0=makeQuery(id+"F39.boolean.opBoolean","MERGE",FACE,{"derivedFrom":[makeQuery(id+"F37.opExtrude","CAP_FACE",FACE,{"disambiguationData":[OSD([sQuery(id+"F36.wireOp",EDGE,"E63.bottom"),sQuery(id+"F36.wireOp",EDGE,"E63.top"),sQuery(id+"F36.wireOp",EDGE,"E63.left"),sQuery(id+"F36.wireOp",EDGE,"E63.right")])],"isStart":false}),makeQuery(id+"F39.opExtrude","CAP_FACE",FACE,{"disambiguationData":[OSD([sQuery(id+"F38.wireOp",EDGE,"E64.bottom"),sQuery(id+"F38.wireOp",EDGE,"E64.top"),sQuery(id+"F38.wireOp",EDGE,"E64.left"),sQuery(id+"F38.wireOp",EDGE,"E64.right")])],"isStart":false}),makeQuery(id+"F39.opExtrude","CAP_FACE",FACE,{"disambiguationData":[OSD([sQuery(id+"F38.wireOp",EDGE,"E65.bottom"),sQuery(id+"F38.wireOp",EDGE,"E65.top"),sQuery(id+"F38.wireOp",EDGE,"E65.left"),sQuery(id+"F38.wireOp",EDGE,"E65.right")])],"isStart":false}),makeQuery(id+"F39.opExtrude","CAP_FACE",FACE,{"disambiguationData":[OSD([sQuery(id+"F38.wireOp",EDGE,"E66.MirrorCS"),sQuery(id+"F38.wireOp",EDGE,"E68.MirrorCS"),sQuery(id+"F38.wireOp",EDGE,"E71.MirrorCS"),sQuery(id+"F38.wireOp",EDGE,"E72.MirrorCS")])],"isStart":false}),makeQuery(id+"F39.opExtrude","CAP_FACE",FACE,{"disambiguationData":[OSD([sQuery(id+"F38.wireOp",EDGE,"E67.MirrorCS"),sQuery(id+"F38.wireOp",EDGE,"E69.MirrorCS"),sQuery(id+"F38.wireOp",EDGE,"E70.MirrorCS"),sQuery(id+"F38.wireOp",EDGE,"E73.MirrorCS")])],"isStart":false})]});
            cPlane(context, id + "F61", {"entities" : qUnion([Q0]), "cplaneType" : CPlaneType.OFFSET, "offset" : 7 * mm, "width" : 150 * mm, "height" : 150 * mm});
        }
        {
            var Q0;
            Q0=qCreatedBy(id+"F61.planeOp",FACE);
            var sketch = newSketch(context, id + "F62", { "sketchPlane" : qUnion([Q0])});
            skLineSegment(sketch, "E128.bottom", {"start": v(-105, -48) * mm, "end": v(105, -48) * mm});
            skLineSegment(sketch, "E128.top", {"start": v(-105, -128) * mm, "end": v(105, -128) * mm});
            skLineSegment(sketch, "E128.left", {"start": v(-105, -48) * mm, "end": v(-105, -128) * mm});
            skLineSegment(sketch, "E128.right", {"start": v(105, -48) * mm, "end": v(105, -128) * mm});
            skCircle(sketch, "E129", {"center": v(0, -88) * mm, "radius": 30 * mm});
            skSolve(sketch);
        }
        {
            var Q0;
            Q0=makeQuery(id+"F62.imprint","IMPRINT",FACE,{"disambiguationData":[TD([[makeQuery(id+"F62.imprint","IMPRINT",EDGE,{"derivedFrom":sQuery(id+"F62.wireOp",EDGE,"E128.bottom")}),-1.0]])]});
            extrude(context, id + "F63", {"entities" : qUnion([Q0]), "depth" : 3 * mm, "offsetDistance" : 25 * mm});
        }
        {
            var Q0;
            Q0=qCreatedBy(id+"F61.planeOp",FACE);
            var sketch = newSketch(context, id + "F64", { "sketchPlane" : qUnion([Q0])});
            skLineSegment(sketch, "E130.bottom", {"start": v(-105, 48) * mm, "end": v(105, 48) * mm});
            skLineSegment(sketch, "E130.top", {"start": v(-105, 131) * mm, "end": v(105, 131) * mm});
            skLineSegment(sketch, "E130.left", {"start": v(-105, 48) * mm, "end": v(-105, 131) * mm});
            skLineSegment(sketch, "E130.right", {"start": v(105, 48) * mm, "end": v(105, 131) * mm});
            skCircle(sketch, "E131", {"center": v(0, 88) * mm, "radius": 30 * mm});
            skSolve(sketch);
        }
        {
            var Q0;
            Q0 = qSketchRegion(id + "F64", true);
            extrude(context, id + "F65", {"entities" : qUnion([Q0]), "depth" : 3 * mm, "offsetDistance" : 25 * mm});
        }
        {
            var Q0;
            Q0=makeQuery(id+"F53.opExtrude","SWEPT_EDGE",EDGE,{"disambiguationData":[OSD([sQuery(id+"F52.wireOp",EDGE,"E111"),sQuery(id+"F52.wireOp",EDGE,"E112")])]});
            var Q1;
            Q1=makeQuery(id+"F53.opExtrude","SWEPT_EDGE",EDGE,{"disambiguationData":[OSD([sQuery(id+"F52.wireOp",EDGE,"E113.MirrorCS"),sQuery(id+"F52.wireOp",EDGE,"E114.MirrorCS")])]});
            chamfer(context, id + "F66", {"entities" : qUnion([Q0, Q1]), "width" : 32 * mm, "tangentPropagation" : true});
        }
        {
            var Q0;
            Q0=qCreatedBy(makeId("Front.planeOp"),FACE);
            cPlane(context, id + "F67", {"entities" : qUnion([Q0]), "cplaneType" : CPlaneType.OFFSET, "offset" : 120 * mm, "oppositeDirection" : true, "width" : 150 * mm, "height" : 150 * mm});
        }
        {
            var Q0;
            Q0=qCreatedBy(id+"F67.planeOp",FACE);
            var sketch = newSketch(context, id + "F68", { "sketchPlane" : qUnion([Q0])});
            skLineSegment(sketch, "E132.bottom", {"start": v(105, 73) * mm, "end": v(-105, 73) * mm});
            skLineSegment(sketch, "E132.top", {"start": v(105, -43) * mm, "end": v(-105, -43) * mm});
            skLineSegment(sketch, "E132.left", {"start": v(105, 73) * mm, "end": v(105, -43) * mm});
            skLineSegment(sketch, "E132.right", {"start": v(-105, 73) * mm, "end": v(-105, -43) * mm});
            skCircle(sketch, "E133", {"center": v(62, 4) * mm, "radius": 30 * mm});
            skCircle(sketch, "E134.MirrorC", {"center": v(-62, 4) * mm, "radius": 30 * mm});
            skSolve(sketch);
        }
        {
            var Q0;
            Q0 = qSketchRegion(id + "F68", true);
            extrude(context, id + "F69", {"entities" : qUnion([Q0]), "oppositeDirection" : true, "depth" : 3 * mm, "offsetDistance" : 25 * mm});
        }
        {
            var Q0;
            Q0=makeQuery(id+"F56.opExtrude","SWEPT_EDGE",EDGE,{"disambiguationData":[OSD([sQuery(id+"F55.wireOp",EDGE,"E127.bottom"),sQuery(id+"F55.wireOp",EDGE,"E127.right")])]});
            var Q1;
            Q1=makeQuery(id+"F57.opPattern","COPY",EDGE,{"derivedFrom":makeQuery(id+"F56.opExtrude","SWEPT_EDGE",EDGE,{"disambiguationData":[OSD([sQuery(id+"F55.wireOp",EDGE,"E127.bottom"),sQuery(id+"F55.wireOp",EDGE,"E127.right")])]}),"instanceName":"1"});
            chamfer(context, id + "F70", {"entities" : qUnion([Q0, Q1]), "width" : 30 * mm, "tangentPropagation" : true});
        }
        {
            var Q0;
            Q0=makeQuery(id+"F56.opExtrude","SWEPT_EDGE",EDGE,{"disambiguationData":[OSD([sQuery(id+"F55.wireOp",EDGE,"E127.top"),sQuery(id+"F55.wireOp",EDGE,"E127.right")])]});
            var Q1;
            Q1=makeQuery(id+"F57.opPattern","COPY",EDGE,{"derivedFrom":makeQuery(id+"F56.opExtrude","SWEPT_EDGE",EDGE,{"disambiguationData":[OSD([sQuery(id+"F55.wireOp",EDGE,"E127.top"),sQuery(id+"F55.wireOp",EDGE,"E127.right")])]}),"instanceName":"1"});
            chamfer(context, id + "F71", {"entities" : qUnion([Q0, Q1]), "width" : 30 * mm, "tangentPropagation" : true});
        }
        {
            var Q0;
            Q0=makeQuery(id+"F53.opExtrude","SWEPT_FACE",FACE,{"disambiguationData":[OSD([sQuery(id+"F52.wireOp",EDGE,"E110.top")])]});
            var sketch = newSketch(context, id + "F72", { "sketchPlane" : qUnion([Q0])});
            skLineSegment(sketch, "E135.bottom", {"start": v(105, 15) * mm, "end": v(-105, 15) * mm});
            skLineSegment(sketch, "E135.top", {"start": v(105, -58) * mm, "end": v(-105, -58) * mm});
            skLineSegment(sketch, "E135.left", {"start": v(105, 15) * mm, "end": v(105, -58) * mm});
            skLineSegment(sketch, "E135.right", {"start": v(-105, 15) * mm, "end": v(-105, -58) * mm});
            skSolve(sketch);
        }
        {
            var Q0;
            Q0 = qSketchRegion(id + "F72", true);
            extrude(context, id + "F73", {"entities" : qUnion([Q0]), "oppositeDirection" : true, "depth" : 3 * mm, "offsetDistance" : 25 * mm});
        }
        {
            var Q0;
            Q0=qCreatedBy(makeId("Right.planeOp"),FACE);
            var sketch = newSketch(context, id + "F74", { "sketchPlane" : qUnion([Q0])});
            skLineSegment(sketch, "E136.bottom", {"start": v(-45, 10) * mm, "end": v(55, 10) * mm});
            skLineSegment(sketch, "E136.top", {"start": v(-45, 2) * mm, "end": v(55, 2) * mm});
            skLineSegment(sketch, "E136.left", {"start": v(-45, 10) * mm, "end": v(-45, 2) * mm});
            skLineSegment(sketch, "E136.right", {"start": v(55, 10) * mm, "end": v(55, 2) * mm});
            skLineSegment(sketch, "E137.bottom", {"start": v(-30, -13) * mm, "end": v(70, -13) * mm});
            skLineSegment(sketch, "E137.top", {"start": v(-30, -21) * mm, "end": v(70, -21) * mm});
            skLineSegment(sketch, "E137.left", {"start": v(-30, -13) * mm, "end": v(-30, -21) * mm});
            skLineSegment(sketch, "E137.right", {"start": v(70, -13) * mm, "end": v(70, -21) * mm});
            skLineSegment(sketch, "E138.bottom", {"start": v(-15, -36) * mm, "end": v(85, -36) * mm});
            skLineSegment(sketch, "E138.top", {"start": v(-15, -44) * mm, "end": v(85, -44) * mm});
            skLineSegment(sketch, "E138.left", {"start": v(-15, -36) * mm, "end": v(-15, -44) * mm});
            skLineSegment(sketch, "E138.right", {"start": v(85, -36) * mm, "end": v(85, -44) * mm});
            skSolve(sketch);
        }
        {
            var Q0;
            Q0 = qSketchRegion(id + "F74", true);
            extrude(context, id + "F75", {"entities" : qUnion([Q0]), "operationType" : NewBodyOperationType.REMOVE, "endBound" : BoundingType.SYMMETRIC, "oppositeDirection" : true, "depth" : 500 * mm, "offsetDistance" : 25 * mm});
        }
        {
            var Q0;
            {var subQ0=sQuery(id+"F55.wireOp",EDGE,"E127.top");Q0=makeQuery(id+"F59.opChamfer","BLEND_EDGE",EDGE,{"blendedFrom":[makeQuery(id+"F56.opExtrude","SWEPT_EDGE",EDGE,{"disambiguationData":[OSD([subQ0,sQuery(id+"F55.wireOp",EDGE,"E127.left")])]}),makeQuery(id+"F56.opExtrude","SWEPT_FACE",FACE,{"disambiguationData":[OSD([subQ0])]})],"blendedInto":[makeQuery(id+"F56.opExtrude","SWEPT_FACE",FACE,{"disambiguationData":[OSD([subQ0])]})]});}
            var Q1;
            {var subQ0=sQuery(id+"F55.wireOp",EDGE,"E127.top");Q1=makeQuery(id+"F60.opChamfer","BLEND_EDGE",EDGE,{"blendedFrom":[makeQuery(id+"F57.opPattern","COPY",EDGE,{"derivedFrom":makeQuery(id+"F56.opExtrude","SWEPT_EDGE",EDGE,{"disambiguationData":[OSD([subQ0,sQuery(id+"F55.wireOp",EDGE,"E127.left")])]}),"instanceName":"1"}),makeQuery(id+"F57.opPattern","COPY",FACE,{"derivedFrom":makeQuery(id+"F56.opExtrude","SWEPT_FACE",FACE,{"disambiguationData":[OSD([subQ0])]}),"instanceName":"1"})],"blendedInto":[makeQuery(id+"F57.opPattern","COPY",FACE,{"derivedFrom":makeQuery(id+"F56.opExtrude","SWEPT_FACE",FACE,{"disambiguationData":[OSD([subQ0])]}),"instanceName":"1"})]});}
            chamfer(context, id + "F76", {"entities" : qUnion([Q0, Q1]), "width" : 45 * mm, "tangentPropagation" : true});
        }
    });
